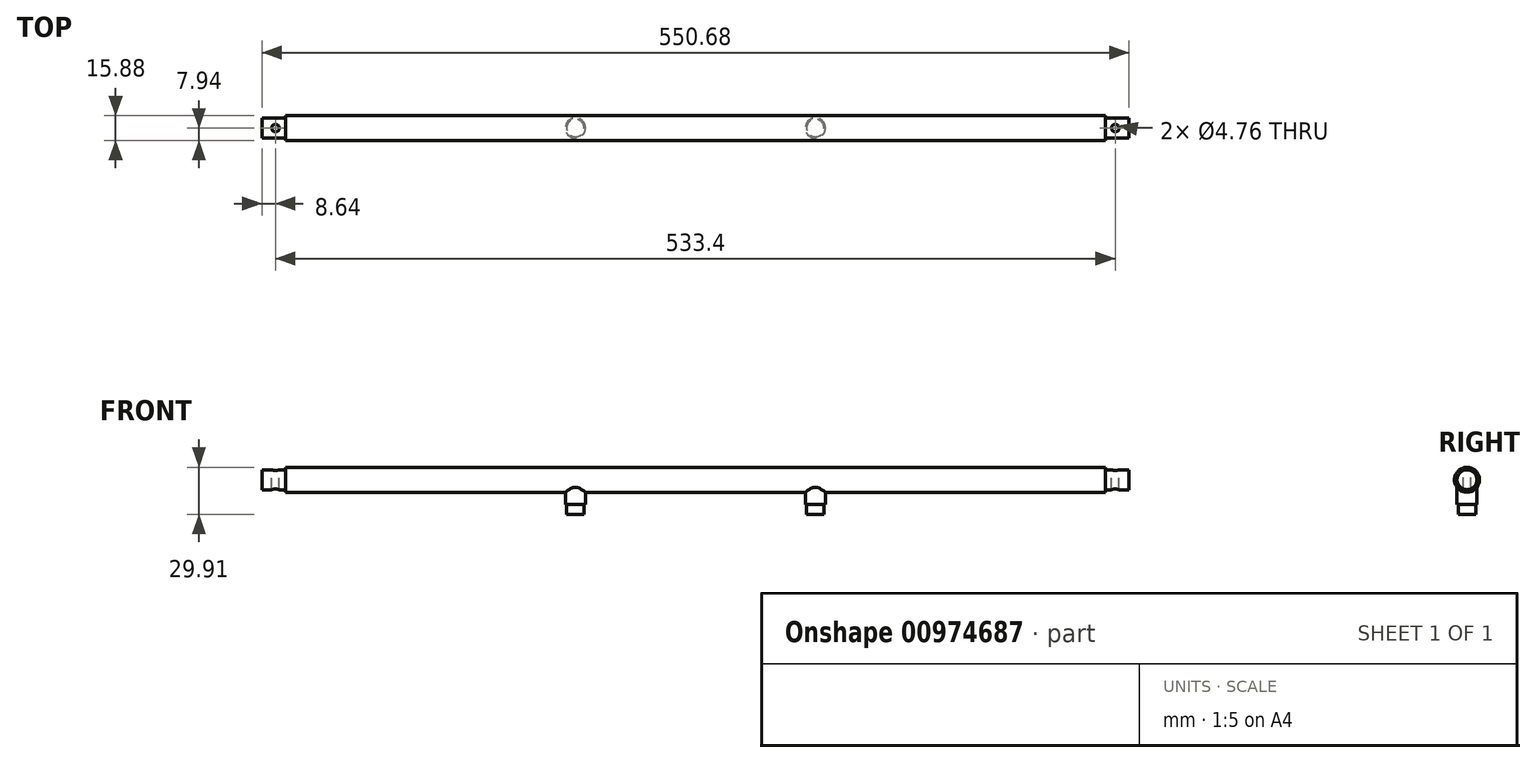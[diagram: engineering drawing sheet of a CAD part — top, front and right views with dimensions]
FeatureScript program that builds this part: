
annotation { "Feature Type Name" : "Feature", "Feature Type Description" : "" }
export const myFeature = defineFeature(function(context is Context, id is Id, definition is map)
    precondition{}
    {
        {
            var Q0;
            Q0=qCreatedBy(makeId("Front.planeOp"),FACE);
            var sketch = newSketch(context, id + "F0", { "sketchPlane" : qUnion([Q0])});
            skLineSegment(sketch, "E0", {"start": v(0, 0) * mm, "end": v(-159.41, 0) * mm, "construction": true});
            skLineSegment(sketch, "E1", {"start": v(14.99, 0) * mm, "end": v(14.99, 6.35) * mm});
            skLineSegment(sketch, "E2", {"start": v(14.99, 6.35) * mm, "end": v(0, 6.35) * mm});
            skLineSegment(sketch, "E3", {"start": v(0, 6.35) * mm, "end": v(0, 7.94) * mm});
            skLineSegment(sketch, "E4", {"start": v(0, 7.94) * mm, "end": v(-520.7, 7.94) * mm});
            skLineSegment(sketch, "E5", {"start": v(-520.7, 7.94) * mm, "end": v(-520.7, 6.35) * mm});
            skLineSegment(sketch, "E6", {"start": v(-520.7, 6.35) * mm, "end": v(-535.69, 6.35) * mm});
            skLineSegment(sketch, "E7", {"start": v(-535.69, 6.35) * mm, "end": v(-535.69, 0) * mm});
            skLineSegment(sketch, "E8", {"start": v(-535.69, 0) * mm, "end": v(14.99, 0) * mm});
            skSolve(sketch);
        }
        {
            var Q0;
            Q0 = qSketchRegion(id + "F0", true);
            var Q1;
            Q1=sQuery(id+"F0.wireOp",EDGE,"E8");
            revolve(context, id + "F1", {"surfaceOperationType" : NewSurfaceOperationType.NEW, "entities" : qUnion([Q0]), "axis" : qUnion([Q1]), "revolveType" : RevolveType.FULL});
        }
        {
            var Q0;
            Q0=qCreatedBy(makeId("Top.planeOp"),FACE);
            var sketch = newSketch(context, id + "F2", { "sketchPlane" : qUnion([Q0])});
            skCircle(sketch, "E9", {"center": v(6.35, 0) * mm, "radius": 2.38 * mm});
            skCircle(sketch, "E10", {"center": v(-527.05, 0) * mm, "radius": 2.38 * mm});
            skSolve(sketch);
        }
        {
            var Q0;
            Q0 = qSketchRegion(id + "F2", true);
            extrude(context, id + "F3", {"entities" : qUnion([Q0]), "operationType" : NewBodyOperationType.REMOVE, "endBound" : BoundingType.SYMMETRIC, "oppositeDirection" : true, "depth" : 50.8 * mm, "offsetDistance" : 25.4 * mm});
        }
        {
            var Q0;
            Q0=qCreatedBy(makeId("Top.planeOp"),FACE);
            var sketch = newSketch(context, id + "F4", { "sketchPlane" : qUnion([Q0])});
            skLineSegment(sketch, "E11", {"start": v(-260.35, 66.1) * mm, "end": v(-260.35, -67.64) * mm, "construction": true});
            skCircle(sketch, "E12", {"center": v(-336.55, 0) * mm, "radius": 6.35 * mm});
            skCircle(sketch, "E13.MirrorC", {"center": v(-184.15, 0) * mm, "radius": 6.35 * mm});
            skSolve(sketch);
        }
        {
            var Q0;
            Q0 = qSketchRegion(id + "F4", true);
            extrude(context, id + "F5", {"entities" : qUnion([Q0]), "operationType" : NewBodyOperationType.ADD, "oppositeDirection" : true, "depth" : 15.62 * mm, "offsetDistance" : 25.4 * mm});
        }
        {
            var Q0;
            Q0=makeQuery(id+"F5.opExtrude","CAP_FACE",FACE,{"disambiguationData":[OSD([sQuery(id+"F4.wireOp",EDGE,"E12")])],"isStart":false});
            var sketch = newSketch(context, id + "F6", { "sketchPlane" : qUnion([Q0])});
            skCircle(sketch, "E14", {"center": v(-336.55, 0) * mm, "radius": 5.56 * mm});
            skCircle(sketch, "E15", {"center": v(-184.15, 0) * mm, "radius": 5.56 * mm});
            skSolve(sketch);
        }
        {
            var Q0;
            Q0 = qSketchRegion(id + "F6", true);
            extrude(context, id + "F7", {"entities" : qUnion([Q0]), "operationType" : NewBodyOperationType.ADD, "depth" : 6.35 * mm, "offsetDistance" : 25.4 * mm});
        }
    });
